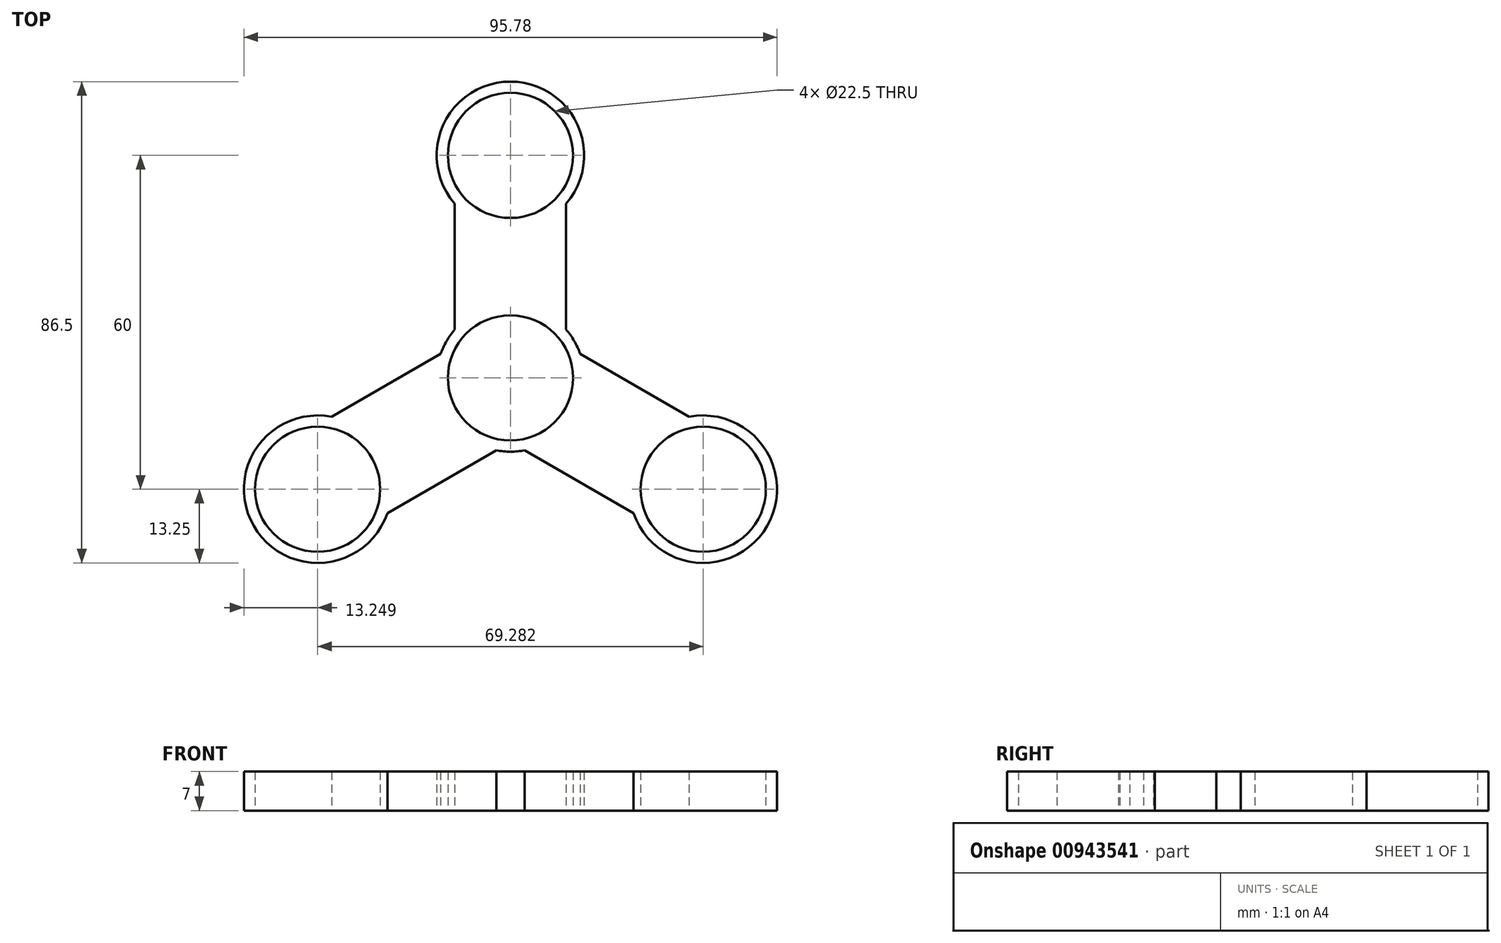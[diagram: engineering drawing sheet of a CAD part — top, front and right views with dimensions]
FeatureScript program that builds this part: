
annotation { "Feature Type Name" : "Feature", "Feature Type Description" : "" }
export const myFeature = defineFeature(function(context is Context, id is Id, definition is map)
    precondition{}
    {
        {
            var Q0;
            Q0=qCreatedBy(makeId("Top.planeOp"),FACE);
            var sketch = newSketch(context, id + "F0", { "sketchPlane" : qUnion([Q0])});
            skCircle(sketch, "E0", {"center": v(0, 0) * mm, "radius": 11.25 * mm});
            skCircle(sketch, "E1.0", {"center": v(0, 0) * mm, "radius": 13.25 * mm});
            skCircle(sketch, "E2", {"center": v(0, 40) * mm, "radius": 11.25 * mm});
            skCircle(sketch, "E3.0", {"center": v(0, 40) * mm, "radius": 13.25 * mm});
            skLineSegment(sketch, "E4", {"start": v(10, 31.3) * mm, "end": v(10, 8.7) * mm});
            skLineSegment(sketch, "E5.MirrorCS", {"start": v(-10, 31.3) * mm, "end": v(-10, 8.7) * mm});
            skCircle(sketch, "E6.1.0", {"center": v(-34.64, -20) * mm, "radius": 11.25 * mm});
            skCircle(sketch, "E6.1.1", {"center": v(-34.64, -20) * mm, "radius": 13.25 * mm});
            skLineSegment(sketch, "E6.1.2", {"start": v(-22.11, -24.31) * mm, "end": v(-2.53, -13) * mm});
            skLineSegment(sketch, "E6.1.3", {"start": v(-32.11, -7) * mm, "end": v(-12.53, 4.31) * mm});
            skCircle(sketch, "E6.2.0", {"center": v(34.64, -20) * mm, "radius": 11.25 * mm});
            skCircle(sketch, "E6.2.1", {"center": v(34.64, -20) * mm, "radius": 13.25 * mm});
            skLineSegment(sketch, "E6.2.2", {"start": v(32.11, -7) * mm, "end": v(12.53, 4.31) * mm});
            skLineSegment(sketch, "E6.2.3", {"start": v(22.11, -24.31) * mm, "end": v(2.53, -13) * mm});
            skSolve(sketch);
        }
        {
            var Q0;
            Q0 = qSketchRegion(id + "F0", true);
            extrude(context, id + "F1", {"entities" : qUnion([Q0]), "depth" : 7 * mm, "offsetDistance" : 25 * mm});
        }
    });
